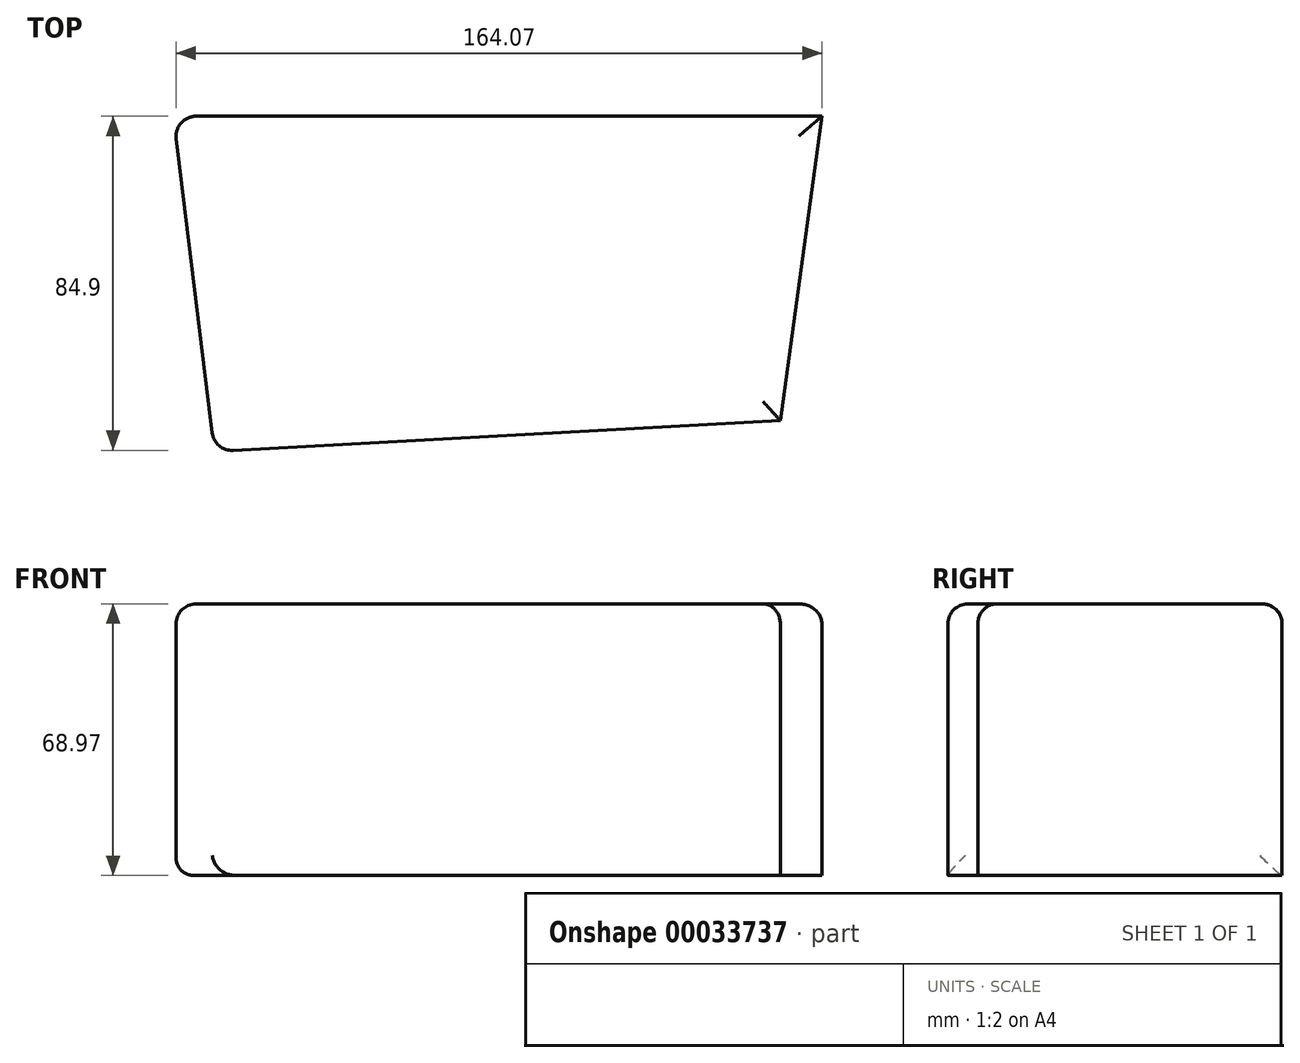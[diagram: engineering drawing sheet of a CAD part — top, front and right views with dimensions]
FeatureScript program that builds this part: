
annotation { "Feature Type Name" : "Feature", "Feature Type Description" : "" }
export const myFeature = defineFeature(function(context is Context, id is Id, definition is map)
    precondition{}
    {
        {
            var Q0;
            Q0=qCreatedBy(makeId("Top.planeOp"),FACE);
            var sketch = newSketch(context, id + "F0", { "sketchPlane" : qUnion([Q0])});
            skLineSegment(sketch, "E0", {"start": v(143.77, 7.85) * mm, "end": v(0, 0) * mm});
            skLineSegment(sketch, "E1", {"start": v(0, 0) * mm, "end": v(-10.38, 85.15) * mm});
            skLineSegment(sketch, "E2", {"start": v(-10.38, 85.15) * mm, "end": v(154.34, 85.15) * mm});
            skLineSegment(sketch, "E3", {"start": v(154.34, 85.15) * mm, "end": v(143.77, 7.85) * mm});
            skSolve(sketch);
        }
        {
            var Q0;
            Q0 = qSketchRegion(id + "F0", true);
            extrude(context, id + "F1", {"entities" : qUnion([Q0]), "depth" : 68.97 * mm});
        }
        {
            var Q0;
            Q0=makeQuery(id+"F1.opExtrude","SWEPT_FACE",FACE,{"disambiguationData":[OSD([sQuery(id+"F0.wireOp",EDGE,"E1")])]});
            var Q1;
            Q1=makeQuery(id+"F1.opExtrude","CAP_FACE",FACE,{"disambiguationData":[OSD([sQuery(id+"F0.wireOp",EDGE,"E0"),sQuery(id+"F0.wireOp",EDGE,"E1"),sQuery(id+"F0.wireOp",EDGE,"E2"),sQuery(id+"F0.wireOp",EDGE,"E3")])],"isStart":false});
            fillet(context, id + "F2", {"entities" : qUnion([Q0, Q1]), "radius" : 5.08 * mm, "tangentPropagation" : true, "allowEdgeOverflow" : false});
        }
    });
